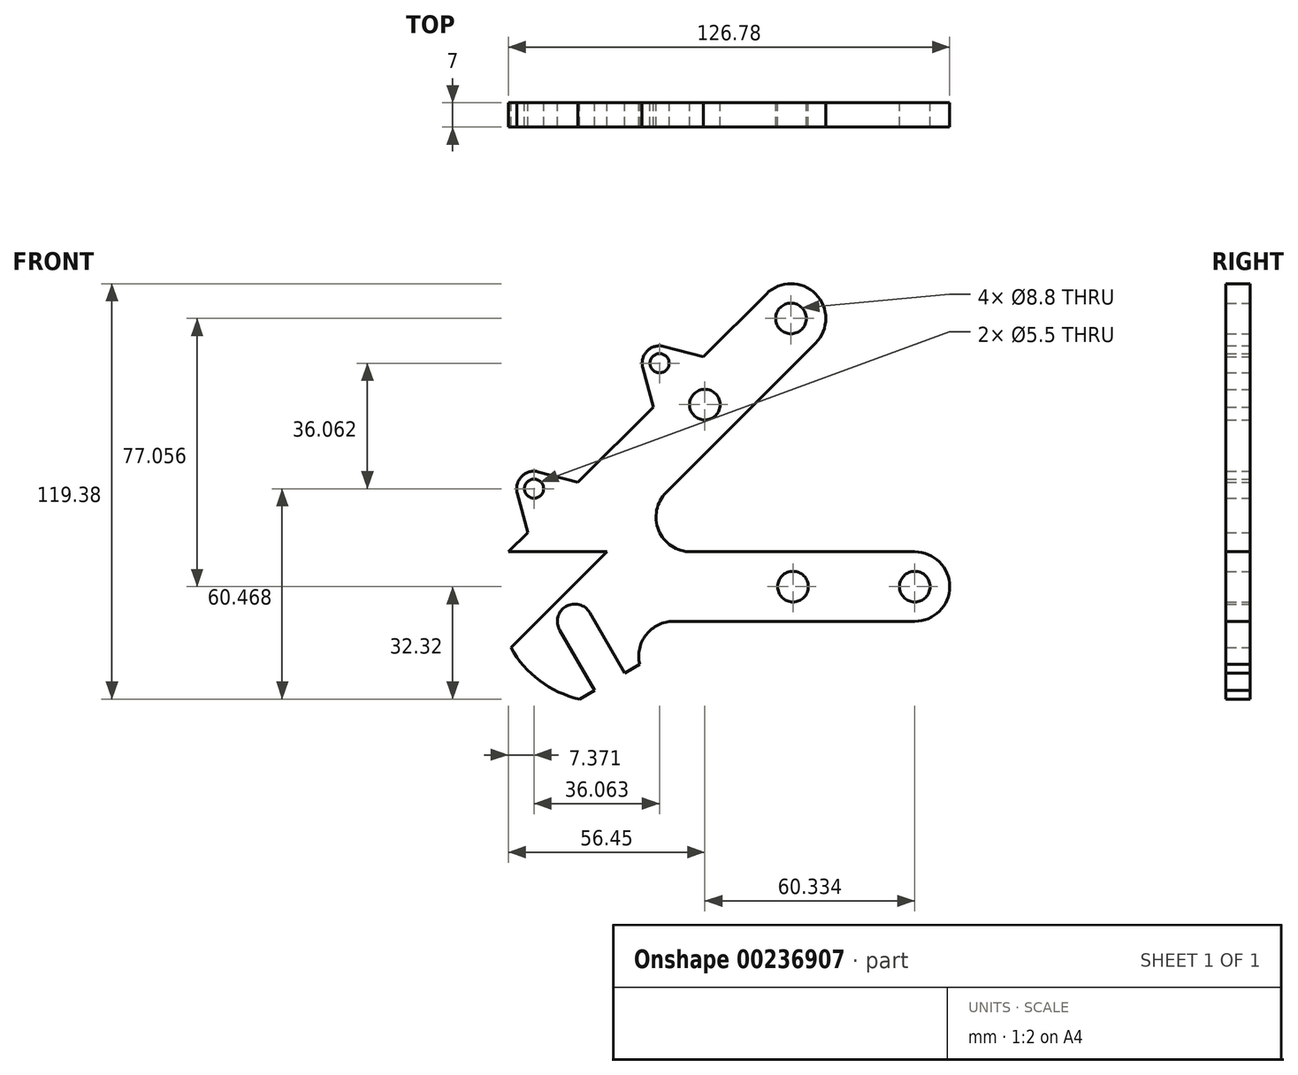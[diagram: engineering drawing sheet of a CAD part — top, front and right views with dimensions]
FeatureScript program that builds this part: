
annotation { "Feature Type Name" : "Feature", "Feature Type Description" : "" }
export const myFeature = defineFeature(function(context is Context, id is Id, definition is map)
    precondition{}
    {
        {
            var Q0;
            Q0=qCreatedBy(makeId("Front.planeOp"),FACE);
            var sketch = newSketch(context, id + "F0", { "sketchPlane" : qUnion([Q0])});
            skLineSegment(sketch, "E0", {"start": v(-20.18, 0) * mm, "end": v(-273.76, 0) * mm, "construction": true});
            skLineSegment(sketch, "E1", {"start": v(-273.76, 0) * mm, "end": v(-273.76, 78.06) * mm, "construction": true});
            skCircle(sketch, "E2", {"center": v(-273.76, 0) * mm, "radius": 5 * mm});
            skLineSegment(sketch, "E3", {"start": v(-273.76, 0) * mm, "end": v(-323.6, 0) * mm, "construction": true});
            skLineSegment(sketch, "E4", {"start": v(-323.6, 0) * mm, "end": v(-285.45, 38.15) * mm, "construction": true});
            skLineSegment(sketch, "E5", {"start": v(-285.45, 38.15) * mm, "end": v(-249.39, 74.21) * mm, "construction": true});
            skLineSegment(sketch, "E6", {"start": v(-249.39, 74.21) * mm, "end": v(-273.76, 0) * mm, "construction": true});
            skLineSegment(sketch, "E7", {"start": v(-285.45, 38.15) * mm, "end": v(-273.76, 0) * mm, "construction": true});
            skLineSegment(sketch, "E8", {"start": v(-273.76, 0) * mm, "end": v(-273.76, -28.91) * mm, "construction": true});
            skLineSegment(sketch, "E9", {"start": v(-273.76, -28.91) * mm, "end": v(-281.76, -28.91) * mm, "construction": true});
            skLineSegment(sketch, "E10", {"start": v(-281.76, -28.91) * mm, "end": v(-273.76, 0) * mm, "construction": true});
            skCircle(sketch, "E11", {"center": v(-281.76, -28.91) * mm, "radius": 4 * mm});
            skLineSegment(sketch, "E12", {"start": v(-273.76, 0) * mm, "end": v(-263.76, -17.32) * mm, "construction": true});
            skCircle(sketch, "E13", {"center": v(-263.76, -17.32) * mm, "radius": 5 * mm});
            skLineSegment(sketch, "E14", {"start": v(-259.43, -14.82) * mm, "end": v(-269.43, 2.5) * mm});
            skLineSegment(sketch, "E15", {"start": v(-268.09, -19.82) * mm, "end": v(-278.09, -2.5) * mm});
            skCircle(sketch, "E16", {"center": v(-281.76, -28.91) * mm, "radius": 7 * mm});
            skLineSegment(sketch, "E17", {"start": v(-288.38, -31.18) * mm, "end": v(-289.45, -35.04) * mm});
            skLineSegment(sketch, "E18", {"start": v(-289.45, -35.04) * mm, "end": v(-282.6, -35.86) * mm});
            skLineSegment(sketch, "E19", {"start": v(-268.09, -19.82) * mm, "end": v(-275.77, -32.53) * mm});
            skCircle(sketch, "E20", {"center": v(-285.45, 38.15) * mm, "radius": 5 * mm});
            skCircle(sketch, "E21", {"center": v(-249.39, 74.21) * mm, "radius": 5 * mm});
            skLineSegment(sketch, "E22", {"start": v(-290.45, 38.02) * mm, "end": v(-288.75, -29.1) * mm});
            skLineSegment(sketch, "E23", {"start": v(-281.91, 41.68) * mm, "end": v(-252.92, 70.68) * mm});
            skLineSegment(sketch, "E24", {"start": v(-261.57, 37.1) * mm, "end": v(-202.28, 96.4) * mm, "construction": true});
            skLineSegment(sketch, "E25", {"start": v(-153.76, 0) * mm, "end": v(-153.76, 35.52) * mm, "construction": true});
            skLineSegment(sketch, "E26", {"start": v(-269.43, 2.5) * mm, "end": v(-244.67, 72.54) * mm});
            skCircle(sketch, "E27", {"center": v(-273.76, 0) * mm, "radius": 30 * mm});
            skSolve(sketch);
        }
        {
            var Q0;
            Q0=qCreatedBy(makeId("Front.planeOp"),FACE);
            var sketch = newSketch(context, id + "F1", { "sketchPlane" : qUnion([Q0])});
            skCircle(sketch, "E28", {"center": v(-176.04, 10) * mm, "radius": 10 * mm});
            skCircle(sketch, "E29", {"center": v(-211.62, 87.06) * mm, "radius": 10 * mm});
            skCircle(sketch, "E30", {"center": v(-273.76, 0) * mm, "radius": 10 * mm});
            skCircle(sketch, "E31", {"center": v(-263.76, -17.32) * mm, "radius": 10 * mm});
            skLineSegment(sketch, "E32", {"start": v(-265.1, 5) * mm, "end": v(-255.1, -12.32) * mm});
            skLineSegment(sketch, "E33", {"start": v(-285.02, -0.49) * mm, "end": v(-272.42, -22.32) * mm});
            skLineSegment(sketch, "E34", {"start": v(-255.1, -12.32) * mm, "end": v(-272.42, -22.32) * mm});
            skLineSegment(sketch, "E35", {"start": v(-273.76, 0) * mm, "end": v(-176.04, 0) * mm});
            skLineSegment(sketch, "E36", {"start": v(-306.67, -22.14) * mm, "end": v(-204.55, 79.98) * mm});
            skLineSegment(sketch, "E37", {"start": v(-351.95, 20) * mm, "end": v(-176.04, 20) * mm});
            skLineSegment(sketch, "E38", {"start": v(-218.7, 94.13) * mm, "end": v(-344.78, -31.96) * mm});
            skCircle(sketch, "E39", {"center": v(-285.45, 38.15) * mm, "radius": 5 * mm});
            skCircle(sketch, "E40", {"center": v(-249.39, 74.21) * mm, "radius": 5 * mm});
            skLineSegment(sketch, "E41", {"start": v(-285.45, 38.15) * mm, "end": v(-280.06, 32.76) * mm, "construction": true});
            skLineSegment(sketch, "E42", {"start": v(-249.39, 74.21) * mm, "end": v(-244, 68.82) * mm, "construction": true});
            skLineSegment(sketch, "E43", {"start": v(-290.28, 36.85) * mm, "end": v(-287.25, 25.57) * mm});
            skLineSegment(sketch, "E44.MirrorCS", {"start": v(-284.16, 42.98) * mm, "end": v(-272.87, 39.95) * mm});
            skLineSegment(sketch, "E45", {"start": v(-254.22, 72.92) * mm, "end": v(-251.2, 61.63) * mm});
            skLineSegment(sketch, "E46.MirrorCS", {"start": v(-248.1, 79.04) * mm, "end": v(-236.8, 76.02) * mm});
            skArc(sketch, "E47", {"start": v(-292.82, 20) * mm, "mid": v(-292.83, -6.08) * mm, "end": v(-272.42, -22.32) * mm});
            skCircle(sketch, "E48", {"center": v(-240.4, 30) * mm, "radius": 10 * mm});
            skCircle(sketch, "E49", {"center": v(-245.37, -10) * mm, "radius": 10 * mm});
            skLineSegment(sketch, "E50", {"start": v(-176.04, 10) * mm, "end": v(-211.04, 10) * mm, "construction": true});
            skLineSegment(sketch, "E51", {"start": v(-211.62, 87.06) * mm, "end": v(-236.37, 62.3) * mm, "construction": true});
            skSolve(sketch);
        }
        {
            var Q0;
            {var subQ0=sQuery(id+"F1.wireOp",EDGE,"E28");var subQ1=makeQuery(id+"F1.imprint","INTERSECT",VERTEX,{"derivedFrom":[subQ0,sQuery(id+"F1.wireOp",EDGE,"E35")]});Q0=makeQuery(id+"F1.imprint","IMPRINT",FACE,{"disambiguationData":[TD([[makeQuery(id+"F1.imprint","IMPRINT",EDGE,{"disambiguationData":[TD([[subQ1,1.0]])],"derivedFrom":subQ0}),1.0]])]});}
            var Q1;
            {var subQ0=sQuery(id+"F1.wireOp",EDGE,"E48");var subQ1=sQuery(id+"F1.wireOp",EDGE,"E36");var subQ2=makeQuery(id+"F1.imprint","INTERSECT",VERTEX,{"derivedFrom":[subQ1,subQ0]});Q1=makeQuery(id+"F1.imprint","IMPRINT",FACE,{"disambiguationData":[TD([[makeQuery(id+"F1.imprint","IMPRINT",EDGE,{"disambiguationData":[TD([[subQ2,1.0]])],"derivedFrom":subQ1}),-1.0]])]});}
            var Q2;
            {var subQ0=sQuery(id+"F1.wireOp",EDGE,"E34");Q2=makeQuery(id+"F1.imprint","IMPRINT",FACE,{"disambiguationData":[TD([[makeQuery(id+"F1.imprint","IMPRINT",EDGE,{"derivedFrom":subQ0}),-1.0]])]});}
            var Q3;
            {var subQ0=sQuery(id+"F1.wireOp",EDGE,"E35");var subQ1=sQuery(id+"F1.wireOp",EDGE,"E30");var subQ2=makeQuery(id+"F1.imprint","INTERSECT",VERTEX,{"derivedFrom":[subQ1,subQ0]});Q3=makeQuery(id+"F1.imprint","IMPRINT",FACE,{"disambiguationData":[TD([[makeQuery(id+"F1.imprint","IMPRINT",EDGE,{"disambiguationData":[TD([[subQ2,1.0]])],"derivedFrom":subQ1}),-1.0]])]});}
            var Q4;
            {var subQ0=sQuery(id+"F1.wireOp",EDGE,"E33");var subQ1=sQuery(id+"F1.wireOp",EDGE,"E30");var subQ2=makeQuery(id+"F1.imprint","INTERSECT",VERTEX,{"derivedFrom":[subQ1,subQ0]});Q4=makeQuery(id+"F1.imprint","IMPRINT",FACE,{"disambiguationData":[TD([[makeQuery(id+"F1.imprint","IMPRINT",EDGE,{"disambiguationData":[TD([[subQ2,-1.0]])],"derivedFrom":subQ1}),-1.0]])]});}
            var Q5;
            {var subQ0=sQuery(id+"F1.wireOp",EDGE,"E30");var subQ6=makeQuery(id+"F1.imprint","INTERSECT",VERTEX,{"derivedFrom":[subQ0,sQuery(id+"F1.wireOp",EDGE,"E32")]});Q5=makeQuery(id+"F1.imprint","IMPRINT",FACE,{"disambiguationData":[TD([[makeQuery(id+"F1.imprint","IMPRINT",EDGE,{"disambiguationData":[TD([[subQ6,1.0]])],"derivedFrom":subQ0}),1.0]])]});}
            var Q6;
            {var subQ0=sQuery(id+"F1.wireOp",EDGE,"E32");var subQ1=sQuery(id+"F1.wireOp",EDGE,"E30");var subQ2=makeQuery(id+"F1.imprint","INTERSECT",VERTEX,{"derivedFrom":[subQ1,subQ0]});Q6=makeQuery(id+"F1.imprint","IMPRINT",FACE,{"disambiguationData":[TD([[makeQuery(id+"F1.imprint","IMPRINT",EDGE,{"disambiguationData":[TD([[subQ2,1.0]])],"derivedFrom":subQ1}),-1.0]])]});}
            var Q7;
            {var subQ0=sQuery(id+"F1.wireOp",EDGE,"E35");var subQ1=sQuery(id+"F1.wireOp",EDGE,"E28");var subQ2=makeQuery(id+"F1.imprint","INTERSECT",VERTEX,{"derivedFrom":[subQ1,subQ0]});Q7=makeQuery(id+"F1.imprint","IMPRINT",FACE,{"disambiguationData":[TD([[makeQuery(id+"F1.imprint","IMPRINT",EDGE,{"disambiguationData":[TD([[subQ2,1.0]])],"derivedFrom":subQ1}),-1.0]])]});}
            var Q8;
            {var subQ0=sQuery(id+"F1.wireOp",EDGE,"E36");var subQ1=sQuery(id+"F1.wireOp",EDGE,"E30");var subQ2=makeQuery(id+"F1.imprint","INTERSECT",VERTEX,{"disambiguationData":[OD(0.0)],"derivedFrom":[subQ1,subQ0]});Q8=makeQuery(id+"F1.imprint","IMPRINT",FACE,{"disambiguationData":[TD([[makeQuery(id+"F1.imprint","IMPRINT",EDGE,{"disambiguationData":[TD([[subQ2,-1.0]])],"derivedFrom":subQ1}),1.0]])]});}
            var Q9;
            {var subQ0=sQuery(id+"F1.wireOp",EDGE,"E33");var subQ1=sQuery(id+"F1.wireOp",EDGE,"E30");var subQ2=makeQuery(id+"F1.imprint","INTERSECT",VERTEX,{"derivedFrom":[subQ1,subQ0]});Q9=makeQuery(id+"F1.imprint","IMPRINT",FACE,{"disambiguationData":[TD([[makeQuery(id+"F1.imprint","IMPRINT",EDGE,{"disambiguationData":[TD([[subQ2,1.0]])],"derivedFrom":subQ1}),-1.0]])]});}
            var Q10;
            {var subQ0=sQuery(id+"F1.wireOp",EDGE,"E47");Q10=makeQuery(id+"F1.imprint","IMPRINT",FACE,{"disambiguationData":[TD([[makeQuery(id+"F1.imprint","IMPRINT",EDGE,{"derivedFrom":subQ0}),1.0]])]});}
            var Q11;
            {var subQ3=sQuery(id+"F1.wireOp",EDGE,"E36");var subQ5=sQuery(id+"F1.wireOp",EDGE,"E29");var subQ6=makeQuery(id+"F1.imprint","INTERSECT",VERTEX,{"derivedFrom":[subQ5,subQ3]});Q11=makeQuery(id+"F1.imprint","IMPRINT",FACE,{"disambiguationData":[TD([[makeQuery(id+"F1.imprint","IMPRINT",EDGE,{"disambiguationData":[TD([[subQ6,1.0]])],"derivedFrom":subQ5}),-1.0]])]});}
            var Q12;
            {var subQ0=sQuery(id+"F1.wireOp",EDGE,"E43");Q12=makeQuery(id+"F1.imprint","IMPRINT",FACE,{"disambiguationData":[TD([[makeQuery(id+"F1.imprint","IMPRINT",EDGE,{"derivedFrom":subQ0}),1.0]])]});}
            var Q13;
            {var subQ0=sQuery(id+"F1.wireOp",EDGE,"E39");var subQ1=makeQuery(id+"F1.imprint","INTERSECT",VERTEX,{"derivedFrom":[subQ0,sQuery(id+"F1.wireOp",EDGE,"E43")]});Q13=makeQuery(id+"F1.imprint","IMPRINT",FACE,{"disambiguationData":[TD([[makeQuery(id+"F1.imprint","IMPRINT",EDGE,{"disambiguationData":[TD([[subQ1,1.0]])],"derivedFrom":subQ0}),1.0]])]});}
            var Q14;
            {var subQ0=sQuery(id+"F1.wireOp",EDGE,"E45");Q14=makeQuery(id+"F1.imprint","IMPRINT",FACE,{"disambiguationData":[TD([[makeQuery(id+"F1.imprint","IMPRINT",EDGE,{"derivedFrom":subQ0}),1.0]])]});}
            var Q15;
            {var subQ0=sQuery(id+"F1.wireOp",EDGE,"E40");var subQ1=makeQuery(id+"F1.imprint","INTERSECT",VERTEX,{"derivedFrom":[subQ0,sQuery(id+"F1.wireOp",EDGE,"E45")]});Q15=makeQuery(id+"F1.imprint","IMPRINT",FACE,{"disambiguationData":[TD([[makeQuery(id+"F1.imprint","IMPRINT",EDGE,{"disambiguationData":[TD([[subQ1,1.0]])],"derivedFrom":subQ0}),1.0]])]});}
            var Q16;
            {var subQ0=sQuery(id+"F1.wireOp",EDGE,"E29");var subQ1=makeQuery(id+"F1.imprint","INTERSECT",VERTEX,{"derivedFrom":[subQ0,sQuery(id+"F1.wireOp",EDGE,"E36")]});Q16=makeQuery(id+"F1.imprint","IMPRINT",FACE,{"disambiguationData":[TD([[makeQuery(id+"F1.imprint","IMPRINT",EDGE,{"disambiguationData":[TD([[subQ1,1.0]])],"derivedFrom":subQ0}),1.0]])]});}
            var Q17;
            {var subQ0=sQuery(id+"F1.wireOp",EDGE,"E49");var subQ3=sQuery(id+"F1.wireOp",EDGE,"E35");var subQ5=makeQuery(id+"F1.imprint","INTERSECT",VERTEX,{"derivedFrom":[subQ3,subQ0]});Q17=makeQuery(id+"F1.imprint","IMPRINT",FACE,{"disambiguationData":[TD([[makeQuery(id+"F1.imprint","IMPRINT",EDGE,{"disambiguationData":[TD([[subQ5,1.0]])],"derivedFrom":subQ3}),-1.0]])]});}
            var Q18;
            {var subQ0=sQuery(id+"F1.wireOp",EDGE,"E36");var subQ1=sQuery(id+"F1.wireOp",EDGE,"E30");var subQ2=makeQuery(id+"F1.imprint","INTERSECT",VERTEX,{"disambiguationData":[OD(0.0)],"derivedFrom":[subQ1,subQ0]});Q18=makeQuery(id+"F1.imprint","IMPRINT",FACE,{"disambiguationData":[TD([[makeQuery(id+"F1.imprint","IMPRINT",EDGE,{"disambiguationData":[TD([[subQ2,-1.0]])],"derivedFrom":subQ1}),-1.0]])]});}
            extrude(context, id + "F2", {"entities" : qUnion([Q0, Q1, Q2, Q3, Q4, Q5, Q6, Q7, Q8, Q9, Q10, Q11, Q12, Q13, Q14, Q15, Q16, Q17, Q18]), "depth" : 7 * mm});
        }
        {
            var Q0;
            {var subQ0=sQuery(id+"F0.wireOp",EDGE,"E2");var subQ2=makeQuery(id+"F0.imprint","INTERSECT",VERTEX,{"derivedFrom":[subQ0,sQuery(id+"F0.wireOp",EDGE,"E15")]});Q0=makeQuery(id+"F0.imprint","IMPRINT",FACE,{"disambiguationData":[TD([[makeQuery(id+"F0.imprint","IMPRINT",EDGE,{"disambiguationData":[TD([[subQ2,1.0]])],"derivedFrom":subQ0}),1.0]])]});}
            var Q1;
            {var subQ0=sQuery(id+"F0.wireOp",EDGE,"E14");Q1=makeQuery(id+"F0.imprint","IMPRINT",FACE,{"disambiguationData":[TD([[makeQuery(id+"F0.imprint","IMPRINT",EDGE,{"derivedFrom":subQ0}),1.0]])]});}
            var Q2;
            {var subQ0=sQuery(id+"F0.wireOp",EDGE,"E13");var subQ1=makeQuery(id+"F0.imprint","INTERSECT",VERTEX,{"derivedFrom":[subQ0,sQuery(id+"F0.wireOp",EDGE,"E14")]});Q2=makeQuery(id+"F0.imprint","IMPRINT",FACE,{"disambiguationData":[TD([[makeQuery(id+"F0.imprint","IMPRINT",EDGE,{"disambiguationData":[TD([[subQ1,-1.0]])],"derivedFrom":subQ0}),1.0]])]});}
            extrude(context, id + "F3", {"entities" : qUnion([Q0, Q1, Q2]), "operationType" : NewBodyOperationType.REMOVE, "endBound" : BoundingType.UP_TO_NEXT, "depth" : 25 * mm});
        }
        {
            var Q0;
            Q0=sQuery(id+"F0.wireOp",VERTEX,"E21.center");
            var Q1;
            Q1=sQuery(id+"F0.wireOp",VERTEX,"E20.center");
            var Q2;
            Q2=makeQuery(id+"F2.opExtrude","SWEPT_BODY",BODY,{"disambiguationData":[OSD([sQuery(id+"F1.wireOp",EDGE,"E28"),sQuery(id+"F1.wireOp",EDGE,"E29"),sQuery(id+"F1.wireOp",EDGE,"E33"),sQuery(id+"F1.wireOp",EDGE,"E34"),sQuery(id+"F1.wireOp",EDGE,"E35"),sQuery(id+"F1.wireOp",EDGE,"E36"),sQuery(id+"F1.wireOp",EDGE,"E37"),sQuery(id+"F1.wireOp",EDGE,"E38"),sQuery(id+"F1.wireOp",EDGE,"E39"),sQuery(id+"F1.wireOp",EDGE,"E40"),sQuery(id+"F1.wireOp",EDGE,"E43"),sQuery(id+"F1.wireOp",EDGE,"E44.MirrorCS"),sQuery(id+"F1.wireOp",EDGE,"E45"),sQuery(id+"F1.wireOp",EDGE,"E46.MirrorCS"),sQuery(id+"F1.wireOp",EDGE,"E47"),sQuery(id+"F1.wireOp",EDGE,"E48"),sQuery(id+"F1.wireOp",EDGE,"E49")])]});
            hole(context, id + "F4", {"style" : HoleStyle.SIMPLE, "endStyle" : HoleEndStyle.THROUGH, "oppositeDirection" : true, "standardTappedOrClearance" : lookupTablePath({ "standard" : "ISO", "fit" : "Normal", "size" : "M5", "type" : "Clearance" }), "standardBlindInLast" : lookupTablePath({ "fit" : "Standard", "standard" : "ISO", "size" : "M5", "type" : "Clearance" }), "holeDiameter" : 5.5 * mm, "locations" : qUnion([Q0, Q1]), "scope" : qUnion([Q2]), "isTappedThrough" : true});
        }
        {
            var Q0;
            Q0=sQuery(id+"F1.wireOp",VERTEX,"E28.center");
            var Q1;
            Q1=sQuery(id+"F1.wireOp",VERTEX,"E29.center");
            var Q2;
            Q2=sQuery(id+"F1.wireOp",VERTEX,"E51.end");
            var Q3;
            Q3=sQuery(id+"F1.wireOp",VERTEX,"E50.end");
            var Q4;
            Q4=makeQuery(id+"F2.opExtrude","SWEPT_BODY",BODY,{"disambiguationData":[OSD([sQuery(id+"F1.wireOp",EDGE,"E28"),sQuery(id+"F1.wireOp",EDGE,"E29"),sQuery(id+"F1.wireOp",EDGE,"E33"),sQuery(id+"F1.wireOp",EDGE,"E34"),sQuery(id+"F1.wireOp",EDGE,"E35"),sQuery(id+"F1.wireOp",EDGE,"E36"),sQuery(id+"F1.wireOp",EDGE,"E37"),sQuery(id+"F1.wireOp",EDGE,"E38"),sQuery(id+"F1.wireOp",EDGE,"E39"),sQuery(id+"F1.wireOp",EDGE,"E40"),sQuery(id+"F1.wireOp",EDGE,"E43"),sQuery(id+"F1.wireOp",EDGE,"E44.MirrorCS"),sQuery(id+"F1.wireOp",EDGE,"E45"),sQuery(id+"F1.wireOp",EDGE,"E46.MirrorCS"),sQuery(id+"F1.wireOp",EDGE,"E47"),sQuery(id+"F1.wireOp",EDGE,"E48"),sQuery(id+"F1.wireOp",EDGE,"E49")])]});
            hole(context, id + "F5", {"style" : HoleStyle.SIMPLE, "endStyle" : HoleEndStyle.THROUGH, "oppositeDirection" : true, "standardTappedOrClearance" : lookupTablePath({ "standard" : "ISO", "fit" : "Normal", "size" : "M8", "type" : "Clearance" }), "standardBlindInLast" : lookupTablePath({ "fit" : "Standard", "standard" : "ISO", "size" : "M8", "type" : "Clearance" }), "holeDiameter" : 8.8 * mm, "locations" : qUnion([Q0, Q1, Q2, Q3]), "scope" : qUnion([Q4]), "isTappedThrough" : true});
        }
    });
